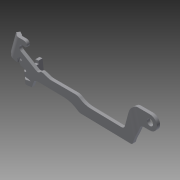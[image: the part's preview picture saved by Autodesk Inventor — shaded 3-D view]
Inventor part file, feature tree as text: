
AUTODESK INVENTOR PART (.ipt)
format: ipt  version: 2014 SP1 (Build 180222100, 222)  size: 4,207,104 bytes
history: native  units: in
note: dims shown in document units (in); Inventor stores cm internally (conversion verified against a paired STEP export)
features: sketch x20, extrude x17, projected_geometry x17, fillet x6, plane x6, other x2
ambient origin geometry x8: Origin, YZ Plane, XZ Plane, XY Plane, X Axis, Y Axis, Z Axis, Center Point
bodies: Solid1 (feature_tree)
feature tree (68):
  other  "Trigger Bar"
  extrude  "Extrusion1"  Depth=3.01in
  sketch  "Sketch2"  dims[d9=0.076in d29=2.8665in d30=0.065in]
  extrude  "Extrusion2"  Depth=2.8665in
  fillet  "Fillet1"  Radius=0.065in
  extrude  "Extrusion3"  Depth=0.1935in
  sketch  "Sketch5"  dims[d83=0.328in d102=0.1055in]
  extrude  "Extrusion4"  TaperAngle=15.0deg  [1 undecoded]
  extrude  "Extrusion5"  Depth=0.1055in
  extrude  "Extrusion6"  Depth=0.0605in TaperAngle=0.0deg
  extrude  "Extrusion7"  Depth=0.0605in
  fillet  "Fillet2"  Radius=0.291in
  fillet  "Fillet3"  Radius=0.08in
  extrude  "Extrusion8"  Depth=0.1105in
  extrude  "Extrusion9"  Depth=0.0605in
  plane  "Work Plane1"
  extrude  "Extrusion10"  Depth=0.0565in TaperAngle=0.0deg
  fillet  "Fillet4"  Radius=0.0565in
  fillet  "Fillet5"  Radius=0.023in
  extrude  "Extrusion11"  Depth=0.005in
  plane  "Work Plane2"
  extrude  "Extrusion12"  Depth=0.102in TaperAngle=0.0deg
  sketch  "Sketch15"  dims[d173=0.0605in d174=0.025in d175=0.0in]
  plane  "Work Plane3"
  extrude  "Extrusion13"  Depth=0.1374in
  plane  "Work Plane4"
  extrude  "Extrusion14"  Depth=0.02in
  plane  "Work Plane6"
  sketch  "Sketch17"  dims[d179=75.0deg d180=1.0in d181=0.0in]
  fillet  "Fillet6"  Radius=0.01in
  extrude  "Extrusion19"  Depth=0.0605in TaperAngle=0.0deg
  extrude  "Extrusion20"  Depth=0.025in TaperAngle=0.0deg
  extrude  "Extrusion21"  Depth=1.0in TaperAngle=0.0deg
  sketch  "Sketch1"  dims[d1=0.1215in d4=3.01in]
  other  "Image1"
  sketch  "Sketch3"  dims[d34=0.0545in d35=0.1935in]
  projected_geometry  "Projected Loop1"
  sketch  "Sketch4"  dims[d37=0.1835in d40=15.0deg]
  projected_geometry  "Projected Loop2"
  sketch  "Sketch6"  dims[d111=0.6647in d133=0.0605in d134=0.0in]
  projected_geometry  "Projected Loop3"
  sketch  "Sketch7"  dims[d141=0.0605in d142=0.0605in d145=0.291in d146=0.0in d147=0.08in]
  sketch  "Sketch8"  dims[d148=0.291in d149=0.0in d150=0.1105in]
  projected_geometry  "Projected Loop4"
  sketch  "Sketch9"  dims[d151=0.0565in d152=0.0in d153=0.0605in]
  projected_geometry  "Projected Loop5"
  sketch  "Sketch10"  dims[d154=0.01in d155=0.0565in d156=0.0in d157=0.0565in d158=0.0in d159=0.023in d160=0.0in]
  projected_geometry  "Projected Loop6"
  sketch  "Sketch11"  dims[d161=0.015in d162=0.005in]
  projected_geometry  "Projected Loop7"
  sketch  "Sketch12"  dims[d163=0.022in d164=0.102in d165=0.0in]
  sketch  "Sketch13"  dims[d166=0.023in d167=0.0in d168=0.1374in]
  sketch  "Sketch14"  dims[d169=0.05in d170=0.0in d171=0.02in d172=0.01in]
  projected_geometry  "Projected Loop8"
  projected_geometry  "Projected Loop9"
  sketch  "Sketch16"  dims[d176=90.0deg d177=0.025in d178=0.0in]
  projected_geometry  "Projected Loop10"
  plane  "Work Plane5"
  sketch  "Sketch19"  dims[d182=0.0605in]
  sketch  "Sketch20"  dims[d183=1.0in d184=0.0in]
  projected_geometry  "Projected Loop11"
  sketch  "Sketch21"  dims[d185=-0.1875in d194=0.125in d195=0.25in d196=0.0in d198=0.079in d199=0.055in d200=0.0in d201=0.055in d202=0.0in]
  projected_geometry  "Projected Loop12"
  projected_geometry  "Project Cut Edges1"
  projected_geometry  "Project Cut Edges2"
  projected_geometry  "Project Cut Edges3"
  projected_geometry  "Project Cut Edges4"
  projected_geometry  "Project Cut Edges6"
note: 1 required parameter value undecoded (feature->parameter linkage not recoverable at this tier; creation-order binding heuristic only, values carry confidence <= 0.55)
